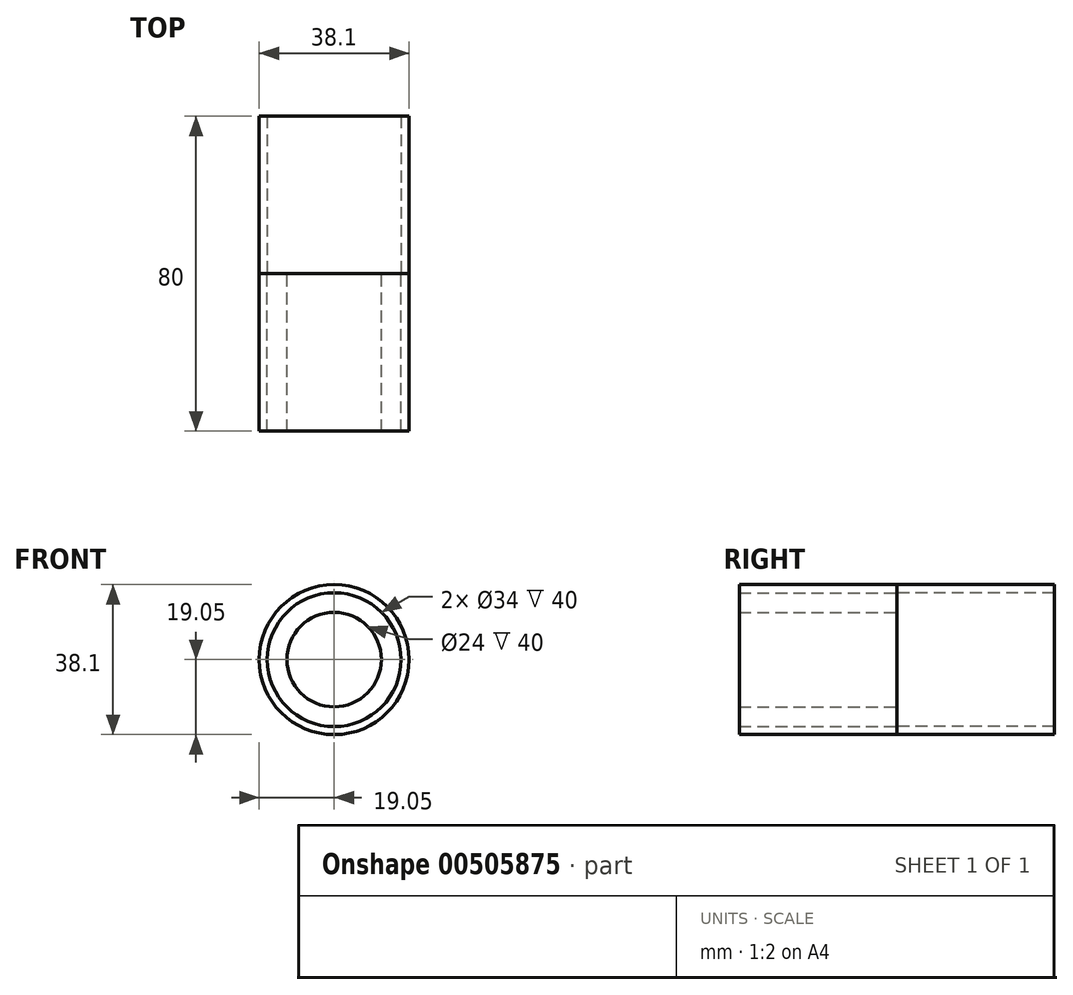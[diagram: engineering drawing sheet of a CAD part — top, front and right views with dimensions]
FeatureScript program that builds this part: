
annotation { "Feature Type Name" : "Feature", "Feature Type Description" : "" }
export const myFeature = defineFeature(function(context is Context, id is Id, definition is map)
    precondition{}
    {
        {
            var Q0;
            Q0=qCreatedBy(makeId("Front.planeOp"),FACE);
            var sketch = newSketch(context, id + "F0", { "sketchPlane" : qUnion([Q0])});
            skCircle(sketch, "E0", {"center": v(0, 0) * mm, "radius": 12 * mm});
            skCircle(sketch, "E1.0", {"center": v(0, 0) * mm, "radius": 17 * mm});
            skCircle(sketch, "E2", {"center": v(0, 0) * mm, "radius": 19.05 * mm});
            skSolve(sketch);
        }
        {
            var Q0;
            Q0=makeQuery(id+"F0.imprint","IMPRINT",FACE,{"disambiguationData":[TD([[makeQuery(id+"F0.imprint","IMPRINT",EDGE,{"derivedFrom":sQuery(id+"F0.wireOp",EDGE,"E0")}),-1.0]])]});
            extrude(context, id + "F1", {"entities" : qUnion([Q0]), "depth" : 40 * mm});
        }
        {
            var Q0;
            Q0=makeQuery(id+"F0.imprint","IMPRINT",FACE,{"disambiguationData":[TD([[makeQuery(id+"F0.imprint","IMPRINT",EDGE,{"derivedFrom":sQuery(id+"F0.wireOp",EDGE,"E1.0")}),-1.0]])]});
            extrude(context, id + "F2", {"entities" : qUnion([Q0]), "oppositeDirection" : true, "depth" : 40 * mm});
        }
        {
            var Q0;
            Q0=makeQuery(id+"F0.imprint","IMPRINT",FACE,{"disambiguationData":[TD([[makeQuery(id+"F0.imprint","IMPRINT",EDGE,{"derivedFrom":sQuery(id+"F0.wireOp",EDGE,"E1.0")}),-1.0]])]});
            extrude(context, id + "F3", {"entities" : qUnion([Q0]), "depth" : 40 * mm});
        }
    });
